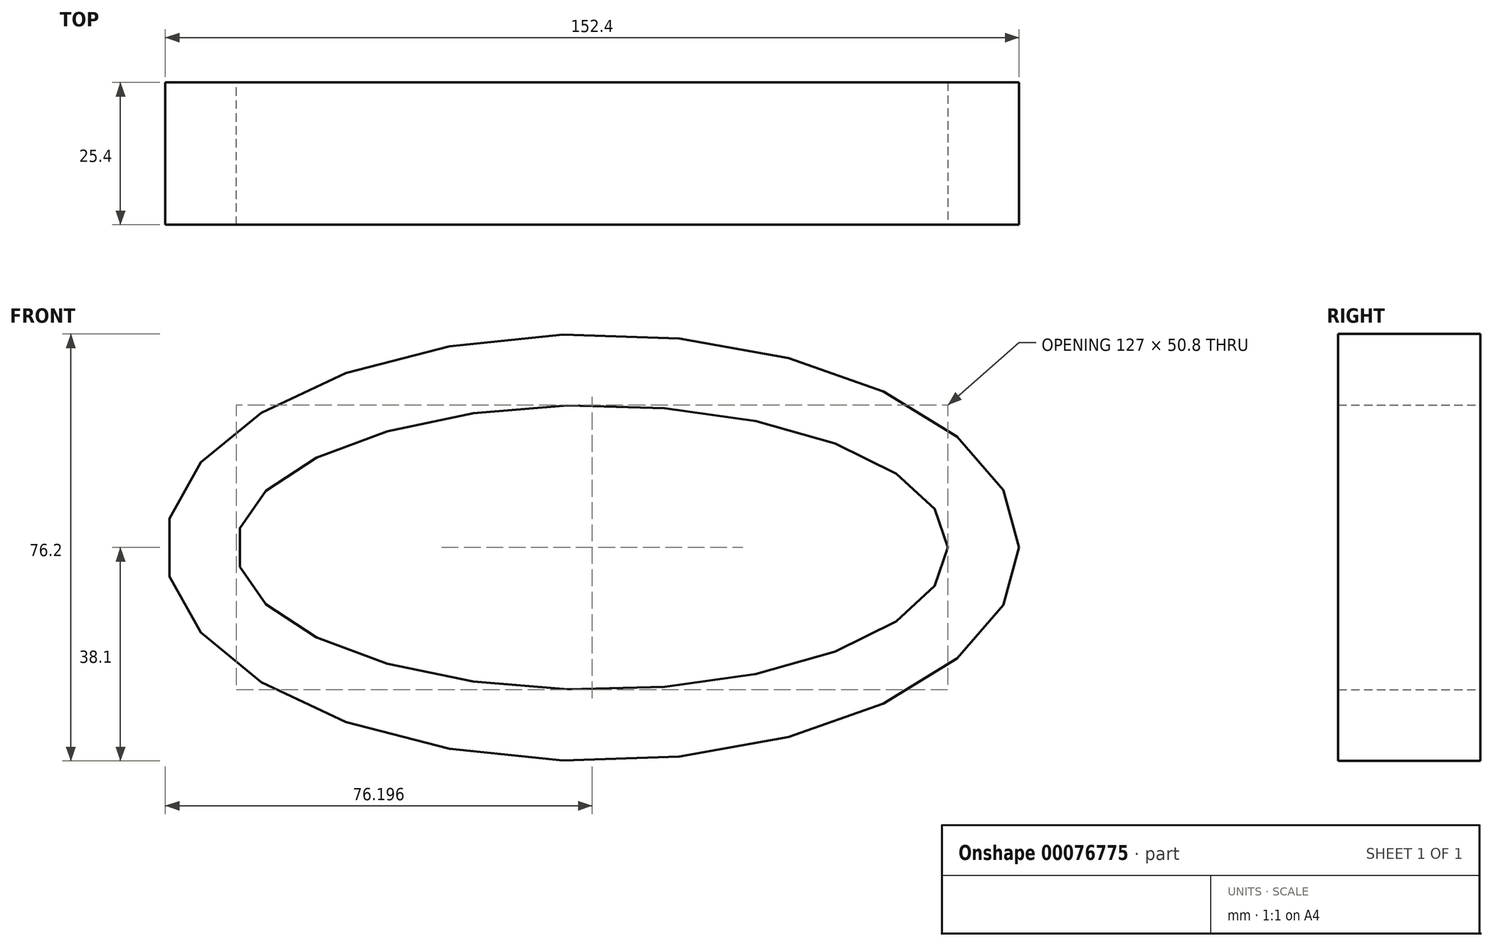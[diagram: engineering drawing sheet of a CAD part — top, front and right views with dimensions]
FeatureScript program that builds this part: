
annotation { "Feature Type Name" : "Feature", "Feature Type Description" : "" }
export const myFeature = defineFeature(function(context is Context, id is Id, definition is map)
    precondition{}
    {
        {
            var Q0;
            Q0=qCreatedBy(makeId("Front.planeOp"),FACE);
            var sketch = newSketch(context, id + "F0", { "sketchPlane" : qUnion([Q0])});
            skEllipse(sketch, "E0", {"center": v(-24.43, 7.31) * mm, "majorRadius": 76.2 * mm, "minorRadius": 38.1 * mm, "majorAxis": v(1, 0)});
            skSolve(sketch);
        }
        {
            var Q0;
            Q0=makeQuery(id+"F0.imprint","IMPRINT",FACE,{"disambiguationData":[TD([[makeQuery(id+"F0.imprint","IMPRINT",EDGE,{"derivedFrom":sQuery(id+"F0.wireOp",EDGE,"E0")}),1.0]])]});
            extrude(context, id + "F1", {"entities" : qUnion([Q0]), "depth" : 25.4 * mm});
        }
        {
            var Q0;
            Q0=makeQuery(id+"F1.opExtrude","CAP_FACE",FACE,{"disambiguationData":[OSD([sQuery(id+"F0.wireOp",EDGE,"E0")])],"isStart":false});
            var sketch = newSketch(context, id + "F2", { "sketchPlane" : qUnion([Q0])});
            skEllipse(sketch, "E1", {"center": v(-24.43, 7.31) * mm, "majorRadius": 63.5 * mm, "minorRadius": 25.4 * mm, "majorAxis": v(1, 0)});
            skSolve(sketch);
        }
        {
            var Q0;
            Q0=makeQuery(id+"F2.imprint","IMPRINT",FACE,{"disambiguationData":[TD([[makeQuery(id+"F2.imprint","IMPRINT",EDGE,{"derivedFrom":sQuery(id+"F2.wireOp",EDGE,"E1")}),1.0]])]});
            extrude(context, id + "F3", {"entities" : qUnion([Q0]), "operationType" : NewBodyOperationType.REMOVE, "endBound" : BoundingType.THROUGH_ALL, "oppositeDirection" : true, "depth" : 25.4 * mm});
        }
    });
